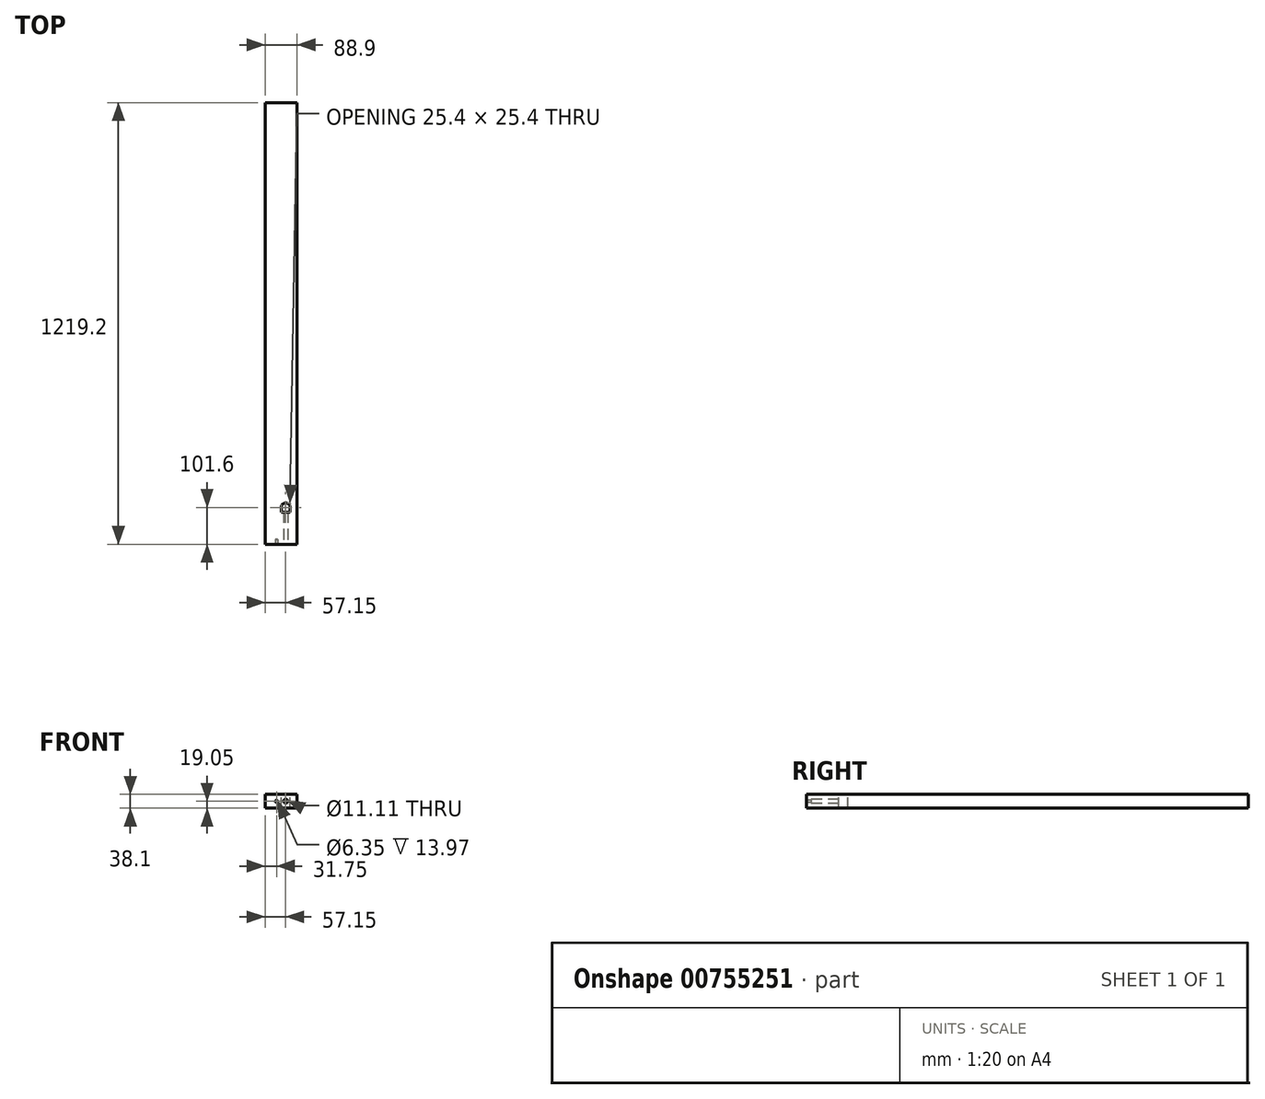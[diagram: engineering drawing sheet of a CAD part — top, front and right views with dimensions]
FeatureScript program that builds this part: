
annotation { "Feature Type Name" : "Feature", "Feature Type Description" : "" }
export const myFeature = defineFeature(function(context is Context, id is Id, definition is map)
    precondition{}
    {
        {
            var Q0;
            Q0=qCreatedBy(makeId("Front.planeOp"),FACE);
            var sketch = newSketch(context, id + "F0", { "sketchPlane" : qUnion([Q0])});
            skLineSegment(sketch, "E0.bottom", {"start": v(0, 0) * mm, "end": v(88.9, 0) * mm});
            skLineSegment(sketch, "E0.top", {"start": v(0, 38.1) * mm, "end": v(88.9, 38.1) * mm});
            skLineSegment(sketch, "E0.left", {"start": v(0, 0) * mm, "end": v(0, 38.1) * mm});
            skLineSegment(sketch, "E0.right", {"start": v(88.9, 0) * mm, "end": v(88.9, 38.1) * mm});
            skSolve(sketch);
        }
        {
            var Q0;
            Q0 = qSketchRegion(id + "F0", true);
            extrude(context, id + "F1", {"entities" : qUnion([Q0]), "depth" : 1219.2 * mm, "offsetDistance" : 25.4 * mm});
        }
        {
            var Q0;
            Q0=makeQuery(id+"F1.opExtrude","CAP_FACE",FACE,{"disambiguationData":[OSD([sQuery(id+"F0.wireOp",EDGE,"E0.bottom"),sQuery(id+"F0.wireOp",EDGE,"E0.top"),sQuery(id+"F0.wireOp",EDGE,"E0.left"),sQuery(id+"F0.wireOp",EDGE,"E0.right")])],"isStart":false});
            var sketch = newSketch(context, id + "F2", { "sketchPlane" : qUnion([Q0])});
            skCircle(sketch, "E1", {"center": v(57.15, 19.05) * mm, "radius": 5.56 * mm});
            skSolve(sketch);
        }
        {
            var Q0;
            Q0 = qSketchRegion(id + "F2", true);
            extrude(context, id + "F3", {"entities" : qUnion([Q0]), "operationType" : NewBodyOperationType.REMOVE, "oppositeDirection" : true, "depth" : 101.6 * mm, "offsetDistance" : 25.4 * mm});
        }
        {
            var Q0;
            Q0=makeQuery(id+"F1.opExtrude","SWEPT_FACE",FACE,{"disambiguationData":[OSD([sQuery(id+"F0.wireOp",EDGE,"E0.top")])]});
            var sketch = newSketch(context, id + "F4", { "sketchPlane" : qUnion([Q0])});
            skLineSegment(sketch, "E2.bottom", {"start": v(44.45, -1117.6) * mm, "end": v(69.85, -1117.6) * mm});
            skLineSegment(sketch, "E2.top", {"start": v(44.45, -1130.3) * mm, "end": v(69.85, -1130.3) * mm});
            skLineSegment(sketch, "E2.left", {"start": v(44.45, -1117.6) * mm, "end": v(44.45, -1130.3) * mm});
            skLineSegment(sketch, "E2.right", {"start": v(69.85, -1117.6) * mm, "end": v(69.85, -1130.3) * mm});
            skArc(sketch, "E3", {"start": v(69.85, -1117.6) * mm, "mid": v(57.15, -1104.9) * mm, "end": v(44.45, -1117.6) * mm});
            skSolve(sketch);
        }
        {
            var Q0;
            Q0 = qSketchRegion(id + "F4", true);
            extrude(context, id + "F5", {"entities" : qUnion([Q0]), "operationType" : NewBodyOperationType.REMOVE, "endBound" : BoundingType.THROUGH_ALL, "oppositeDirection" : true, "depth" : 25.4 * mm, "offsetDistance" : 25.4 * mm});
        }
        {
            var Q0;
            Q0=makeQuery(id+"F1.opExtrude","CAP_FACE",FACE,{"disambiguationData":[OSD([sQuery(id+"F0.wireOp",EDGE,"E0.bottom"),sQuery(id+"F0.wireOp",EDGE,"E0.top"),sQuery(id+"F0.wireOp",EDGE,"E0.left"),sQuery(id+"F0.wireOp",EDGE,"E0.right")])],"isStart":false});
            var sketch = newSketch(context, id + "F6", { "sketchPlane" : qUnion([Q0])});
            skCircle(sketch, "E4", {"center": v(31.75, 19.05) * mm, "radius": 3.18 * mm});
            skSolve(sketch);
        }
        {
            var Q0;
            Q0 = qSketchRegion(id + "F6", true);
            extrude(context, id + "F7", {"entities" : qUnion([Q0]), "operationType" : NewBodyOperationType.REMOVE, "oppositeDirection" : true, "depth" : 13.97 * mm, "offsetDistance" : 25.4 * mm});
        }
        {
            var Q0;
            Q0=qCreatedBy(makeId("Front.planeOp"),FACE);
            cPlane(context, id + "F8", {"entities" : qUnion([Q0]), "cplaneType" : CPlaneType.OFFSET, "offset" : 609.6 * mm, "width" : 152.4 * mm, "height" : 152.4 * mm});
        }
    });
